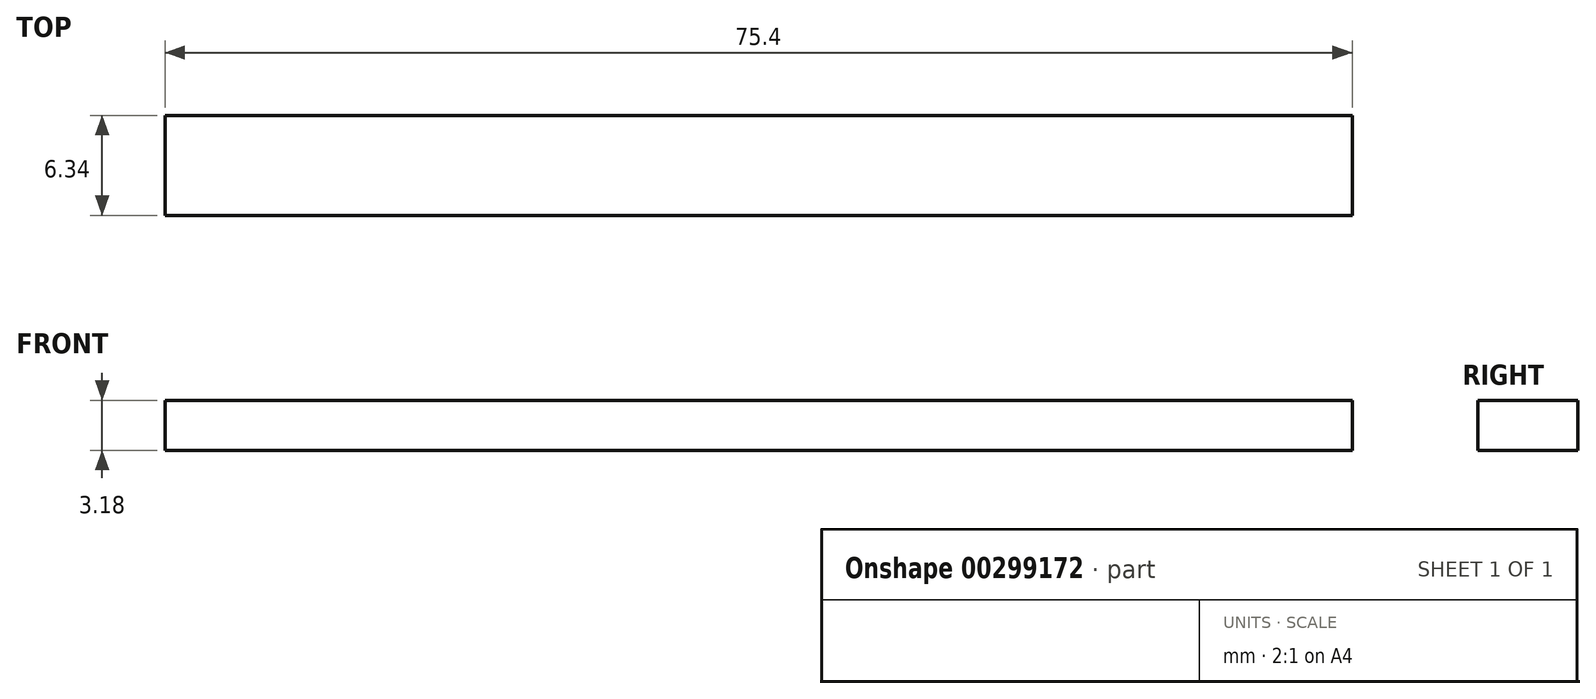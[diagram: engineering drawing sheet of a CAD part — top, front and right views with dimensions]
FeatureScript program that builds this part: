
annotation { "Feature Type Name" : "Feature", "Feature Type Description" : "" }
export const myFeature = defineFeature(function(context is Context, id is Id, definition is map)
    precondition{}
    {
        {
            var Q0;
            Q0=qCreatedBy(makeId("Front.planeOp"),FACE);
            var sketch = newSketch(context, id + "F0", { "sketchPlane" : qUnion([Q0])});
            skLineSegment(sketch, "E0.bottom", {"start": v(37.7, 1.59) * mm, "end": v(-37.7, 1.59) * mm});
            skLineSegment(sketch, "E0.top", {"start": v(37.7, -1.59) * mm, "end": v(-37.7, -1.59) * mm});
            skLineSegment(sketch, "E0.left", {"start": v(37.7, 1.59) * mm, "end": v(37.7, -1.59) * mm});
            skLineSegment(sketch, "E0.right", {"start": v(-37.7, 1.59) * mm, "end": v(-37.7, -1.59) * mm});
            skPoint(sketch, "E0.middle", {"position": v(0, 0) * mm});
            skSolve(sketch);
        }
        {
            var Q0;
            Q0 = qSketchRegion(id + "F0", true);
            extrude(context, id + "F1", {"entities" : qUnion([Q0]), "endBound" : BoundingType.SYMMETRIC, "depth" : 6.35 * mm});
        }
    });
